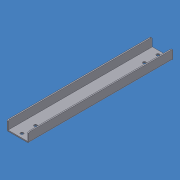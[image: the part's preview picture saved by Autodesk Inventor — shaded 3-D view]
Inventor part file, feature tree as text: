
AUTODESK INVENTOR PART (.ipt)
format: ipt  version: 2015 SP1 (Build 190203100, 203)  size: 180,736 bytes
history: native  units: mm
features: other x6, sheet_metal_op x5, sketch x4, plane x2, mirror x1, chamfer x1
ambient origin geometry x8: Origin, YZ Plane, XZ Plane, XY Plane, X Axis, Y Axis, Z Axis, Center Point
bodies: Solid1 (feature_tree)
feature tree (19):
  sheet_metal_op  "Face1"
  sheet_metal_op  "Flange1"
  sheet_metal_op  "Flange2"
  plane  "Work Plane1"
  mirror  "Mirror1"
  chamfer  "Corner Round1"
  plane  "Work Plane2"
  sketch  "Sketch1"  dims[d2=72.0mm]
  other  "Plate1"
  sketch  "Sketch2"  dims[d3=530.0mm]
  other  "Plate2"
  sheet_metal_op  "Bend1"
  sketch  "Sketch3"  dims[d4=0.001mm]
  other  "Plate3"
  sheet_metal_op  "Bend2"
  sketch  "Sketch4"  dims[d5=4.0mm d6=0.001mm d7=8.0mm d8=0.001mm d9=31.0mm d10=90.0deg d11=0.001mm d12=4.0mm d13=0.001mm d14=8.0mm d15=0.001mm d16=31.0mm d17=90.0deg d18=0.001mm d19=11.0mm d20=11.0mm d21=15.0mm d22=50.0mm d23=4.0mm d24=0.0mm d25=5.0mm d0=4.0mm]
  other  "FlatPattern"
  other  "Cut1"
  other  "FlatPatternExtrusion2"
